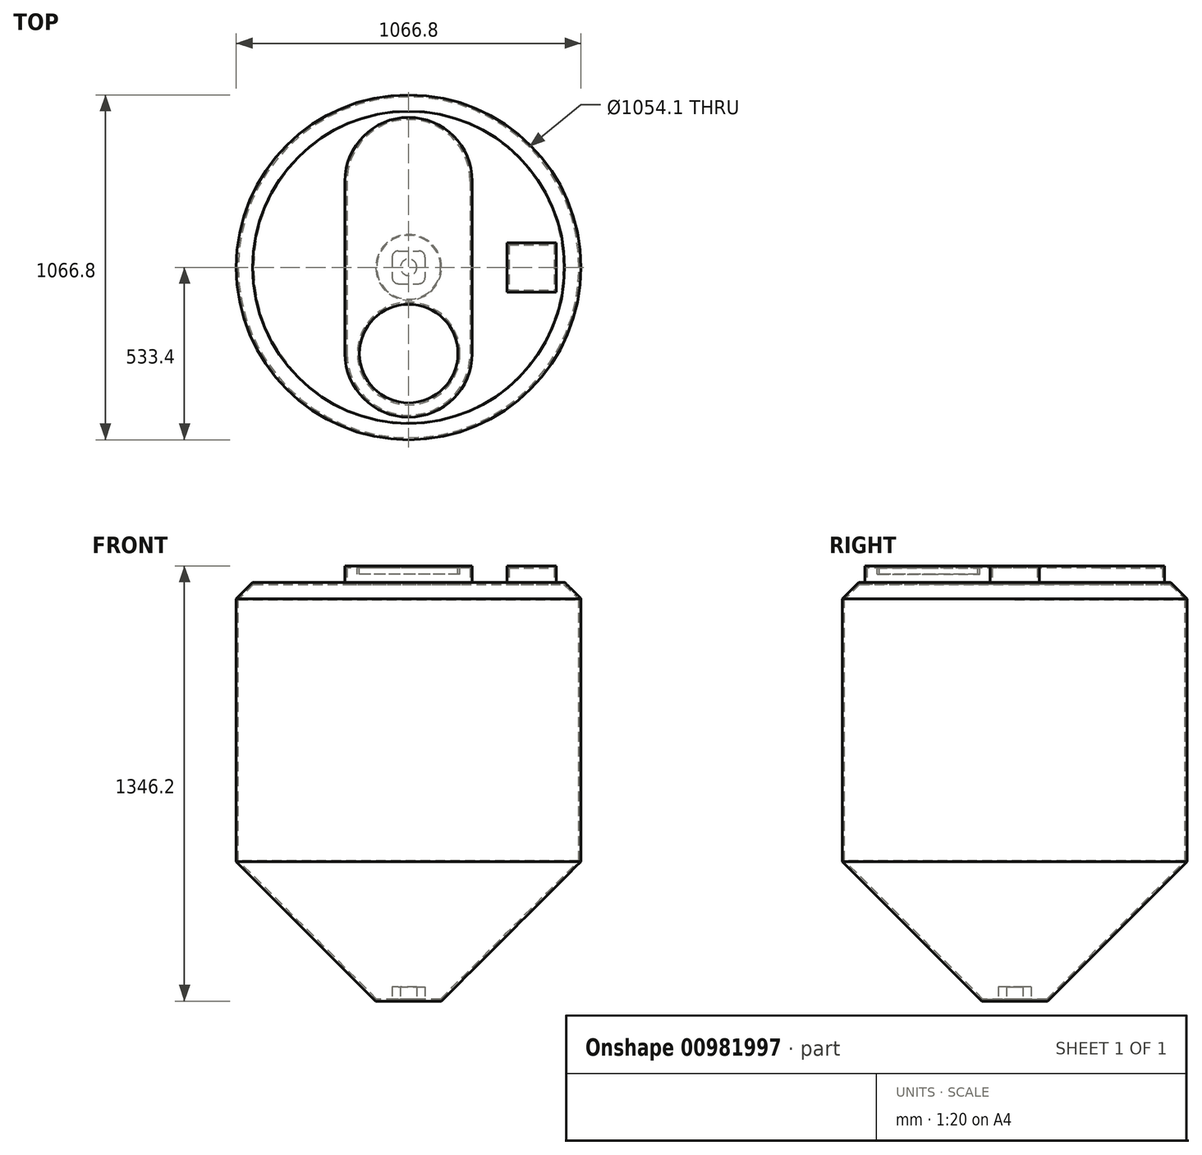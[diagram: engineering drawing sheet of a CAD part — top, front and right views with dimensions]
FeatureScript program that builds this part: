
annotation { "Feature Type Name" : "Feature", "Feature Type Description" : "" }
export const myFeature = defineFeature(function(context is Context, id is Id, definition is map)
    precondition{}
    {
        {
            var Q0;
            Q0=qCreatedBy(makeId("Front.planeOp"),FACE);
            var sketch = newSketch(context, id + "F0", { "sketchPlane" : qUnion([Q0])});
            skLineSegment(sketch, "E0", {"start": v(0, 0) * mm, "end": v(-101.6, 0) * mm});
            skLineSegment(sketch, "E1", {"start": v(-101.6, 0) * mm, "end": v(-533.4, 431.8) * mm});
            skLineSegment(sketch, "E2", {"start": v(-533.4, 431.8) * mm, "end": v(-533.4, 1244.6) * mm});
            skLineSegment(sketch, "E3", {"start": v(-533.4, 1244.6) * mm, "end": v(-482.6, 1295.4) * mm});
            skLineSegment(sketch, "E4", {"start": v(-482.6, 1295.4) * mm, "end": v(0, 1295.4) * mm});
            skLineSegment(sketch, "E5", {"start": v(0, 1295.4) * mm, "end": v(0, 0) * mm});
            skSolve(sketch);
        }
        {
            var Q0;
            Q0 = qSketchRegion(id + "F0", true);
            var Q1;
            Q1=sQuery(id+"F0.wireOp",EDGE,"E5");
            revolve(context, id + "F1", {"surfaceOperationType" : NewSurfaceOperationType.NEW, "entities" : qUnion([Q0]), "axis" : qUnion([Q1]), "revolveType" : RevolveType.FULL});
        }
        {
            var Q0;
            Q0=makeQuery(id+"F1.opRevolve","SWEPT_FACE",FACE,{"disambiguationData":[OSD([sQuery(id+"F0.wireOp",EDGE,"E4")])]});
            var sketch = newSketch(context, id + "F2", { "sketchPlane" : qUnion([Q0])});
            skLineSegment(sketch, "E6.bottom", {"start": v(304.8, 76.2) * mm, "end": v(457.2, 76.2) * mm});
            skLineSegment(sketch, "E6.top", {"start": v(304.8, -76.2) * mm, "end": v(457.2, -76.2) * mm});
            skLineSegment(sketch, "E6.left", {"start": v(304.8, 76.2) * mm, "end": v(304.8, -76.2) * mm});
            skLineSegment(sketch, "E6.right", {"start": v(457.2, 76.2) * mm, "end": v(457.2, -76.2) * mm});
            skLineSegment(sketch, "E7", {"start": v(0, 0) * mm, "end": v(304.8, 0) * mm, "construction": true});
            skSolve(sketch);
        }
        {
            var Q0;
            Q0 = qSketchRegion(id + "F2", true);
            extrude(context, id + "F3", {"entities" : qUnion([Q0]), "operationType" : NewBodyOperationType.ADD, "depth" : 50.8 * mm, "offsetDistance" : 25.4 * mm});
        }
        {
            var Q0;
            Q0=makeQuery(id+"F1.opRevolve","SWEPT_FACE",FACE,{"disambiguationData":[OSD([sQuery(id+"F0.wireOp",EDGE,"E4")])]});
            var sketch = newSketch(context, id + "F4", { "sketchPlane" : qUnion([Q0])});
            skLineSegment(sketch, "E8.bottom", {"start": v(0, 463.55) * mm, "end": v(0, 463.55) * mm});
            skLineSegment(sketch, "E8.top", {"start": v(0, -463.55) * mm, "end": v(0, -463.55) * mm});
            skLineSegment(sketch, "E8.left", {"start": v(-196.85, 266.7) * mm, "end": v(-196.85, -266.7) * mm});
            skLineSegment(sketch, "E8.right", {"start": v(196.85, 266.7) * mm, "end": v(196.85, -266.7) * mm});
            skLineSegment(sketch, "E9", {"start": v(0, 463.55) * mm, "end": v(0, 0) * mm, "construction": true});
            skPoint(sketch, "E10.visualSharp", {"position": v(-196.85, 463.55) * mm});
            skArc(sketch, "E10.filletArc", {"start": v(0, 463.55) * mm, "mid": v(-139.2, 405.9) * mm, "end": v(-196.85, 266.7) * mm});
            skPoint(sketch, "E11.visualSharp", {"position": v(196.85, 463.55) * mm});
            skArc(sketch, "E11.filletArc", {"start": v(196.85, 266.7) * mm, "mid": v(139.2, 405.9) * mm, "end": v(0, 463.55) * mm});
            skPoint(sketch, "E12.visualSharp", {"position": v(196.85, -463.55) * mm});
            skArc(sketch, "E12.filletArc", {"start": v(0, -463.55) * mm, "mid": v(139.2, -405.9) * mm, "end": v(196.85, -266.7) * mm});
            skPoint(sketch, "E13.visualSharp", {"position": v(-196.85, -463.55) * mm});
            skArc(sketch, "E13.filletArc", {"start": v(-196.85, -266.7) * mm, "mid": v(-139.2, -405.9) * mm, "end": v(0, -463.55) * mm});
            skLineSegment(sketch, "E14", {"start": v(-196.85, 0) * mm, "end": v(0, 0) * mm, "construction": true});
            skSolve(sketch);
        }
        {
            var Q0;
            Q0 = qSketchRegion(id + "F4", true);
            extrude(context, id + "F5", {"entities" : qUnion([Q0]), "operationType" : NewBodyOperationType.ADD, "depth" : 50.8 * mm, "offsetDistance" : 25.4 * mm});
        }
        {
            var Q0;
            Q0=makeQuery(id+"F5.opExtrude","CAP_FACE",FACE,{"disambiguationData":[OSD([sQuery(id+"F4.wireOp",EDGE,"E8.left"),sQuery(id+"F4.wireOp",EDGE,"E8.right"),sQuery(id+"F4.wireOp",EDGE,"E10.filletArc"),sQuery(id+"F4.wireOp",EDGE,"E11.filletArc"),sQuery(id+"F4.wireOp",EDGE,"E12.filletArc"),sQuery(id+"F4.wireOp",EDGE,"E13.filletArc")])],"isStart":false});
            var sketch = newSketch(context, id + "F6", { "sketchPlane" : qUnion([Q0])});
            skCircle(sketch, "E15", {"center": v(0, -266.7) * mm, "radius": 152.4 * mm});
            skSolve(sketch);
        }
        {
            var Q0;
            Q0 = qSketchRegion(id + "F6", true);
            extrude(context, id + "F7", {"entities" : qUnion([Q0]), "operationType" : NewBodyOperationType.REMOVE, "oppositeDirection" : true, "depth" : 25.4 * mm, "offsetDistance" : 25.4 * mm});
        }
        {
            var Q0;
            Q0=makeQuery(id+"F7.boolean.opBoolean","COPY",FACE,{"derivedFrom":makeQuery(id+"F7.opExtrude","CAP_FACE",FACE,{"disambiguationData":[OSD([sQuery(id+"F6.wireOp",EDGE,"E15")])],"isStart":false})});
            shell(context, id + "F8", {"entities" : qUnion([Q0]), "thickness" : 6.35 * mm});
        }
        {
            var Q0;
            Q0=makeQuery(id+"F8.opShell","OFFSET_FACE",FACE,{"disambiguationData":[OSD([sQuery(id+"F0.wireOp",EDGE,"E0")])]});
            var sketch = newSketch(context, id + "F9", { "sketchPlane" : qUnion([Q0])});
            skLineSegment(sketch, "E16.bottom", {"start": v(-50.8, 50.8) * mm, "end": v(50.8, 50.8) * mm});
            skLineSegment(sketch, "E16.top", {"start": v(-50.8, -50.8) * mm, "end": v(50.8, -50.8) * mm});
            skLineSegment(sketch, "E16.left", {"start": v(-50.8, 50.8) * mm, "end": v(-50.8, -50.8) * mm});
            skLineSegment(sketch, "E16.right", {"start": v(50.8, 50.8) * mm, "end": v(50.8, -50.8) * mm});
            skLineSegment(sketch, "E17", {"start": v(50.8, 50.8) * mm, "end": v(-50.8, -50.8) * mm, "construction": true});
            skCircle(sketch, "E18", {"center": v(0, 0) * mm, "radius": 25.4 * mm});
            skSolve(sketch);
        }
        {
            var Q0;
            Q0 = qSketchRegion(id + "F9", true);
            extrude(context, id + "F10", {"entities" : qUnion([Q0]), "operationType" : NewBodyOperationType.ADD, "depth" : 38.1 * mm, "offsetDistance" : 25.4 * mm});
        }
        {
            var Q0;
            Q0=makeQuery(id+"F10.opExtrude","SWEPT_EDGE",EDGE,{"disambiguationData":[OSD([sQuery(id+"F9.wireOp",EDGE,"E16.top"),sQuery(id+"F9.wireOp",EDGE,"E16.left")])]});
            var Q1;
            Q1=makeQuery(id+"F10.opExtrude","SWEPT_EDGE",EDGE,{"disambiguationData":[OSD([sQuery(id+"F9.wireOp",EDGE,"E16.top"),sQuery(id+"F9.wireOp",EDGE,"E16.right")])]});
            var Q2;
            Q2=makeQuery(id+"F10.opExtrude","SWEPT_EDGE",EDGE,{"disambiguationData":[OSD([sQuery(id+"F9.wireOp",EDGE,"E16.bottom"),sQuery(id+"F9.wireOp",EDGE,"E16.right")])]});
            var Q3;
            Q3=makeQuery(id+"F10.opExtrude","SWEPT_EDGE",EDGE,{"disambiguationData":[OSD([sQuery(id+"F9.wireOp",EDGE,"E16.bottom"),sQuery(id+"F9.wireOp",EDGE,"E16.left")])]});
            fillet(context, id + "F11", {"entities" : qUnion([Q0, Q1, Q2, Q3]), "radius" : 19.05 * mm, "tangentPropagation" : true, "allowEdgeOverflow" : false});
        }
    });
